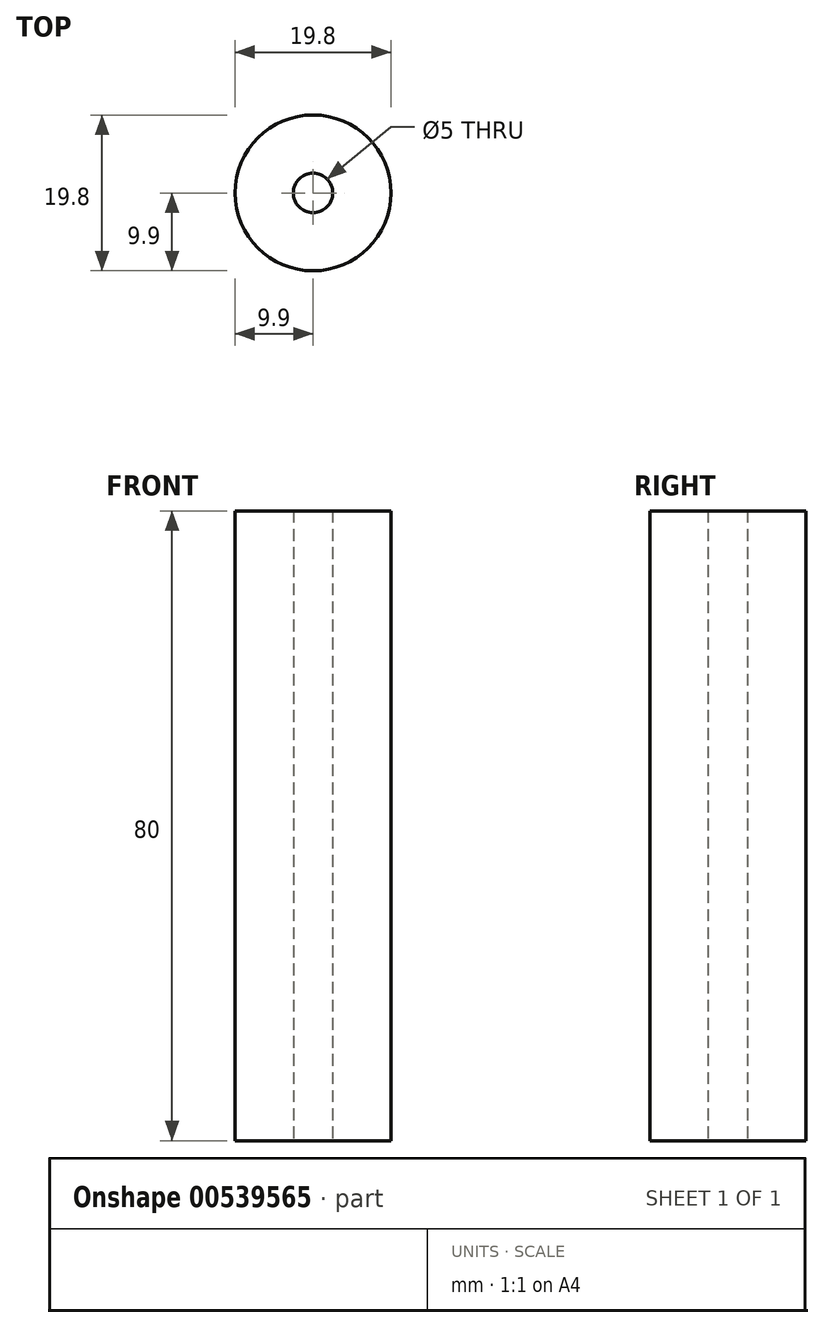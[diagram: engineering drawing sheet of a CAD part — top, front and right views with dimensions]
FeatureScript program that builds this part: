
annotation { "Feature Type Name" : "Feature", "Feature Type Description" : "" }
export const myFeature = defineFeature(function(context is Context, id is Id, definition is map)
    precondition{}
    {
        {
            var Q0;
            Q0=qCreatedBy(makeId("Top.planeOp"),FACE);
            var sketch = newSketch(context, id + "F0", { "sketchPlane" : qUnion([Q0])});
            skCircle(sketch, "E0", {"center": v(0, 0) * mm, "radius": 9.9 * mm});
            skCircle(sketch, "E1", {"center": v(0, 0) * mm, "radius": 2.5 * mm});
            skSolve(sketch);
        }
        {
            var Q0;
            Q0=makeQuery(id+"F0.imprint","IMPRINT",FACE,{"disambiguationData":[TD([[makeQuery(id+"F0.imprint","IMPRINT",EDGE,{"derivedFrom":sQuery(id+"F0.wireOp",EDGE,"E0")}),1.0]])]});
            extrude(context, id + "F1", {"entities" : qUnion([Q0]), "depth" : 80 * mm, "offsetDistance" : 25 * mm});
        }
    });
